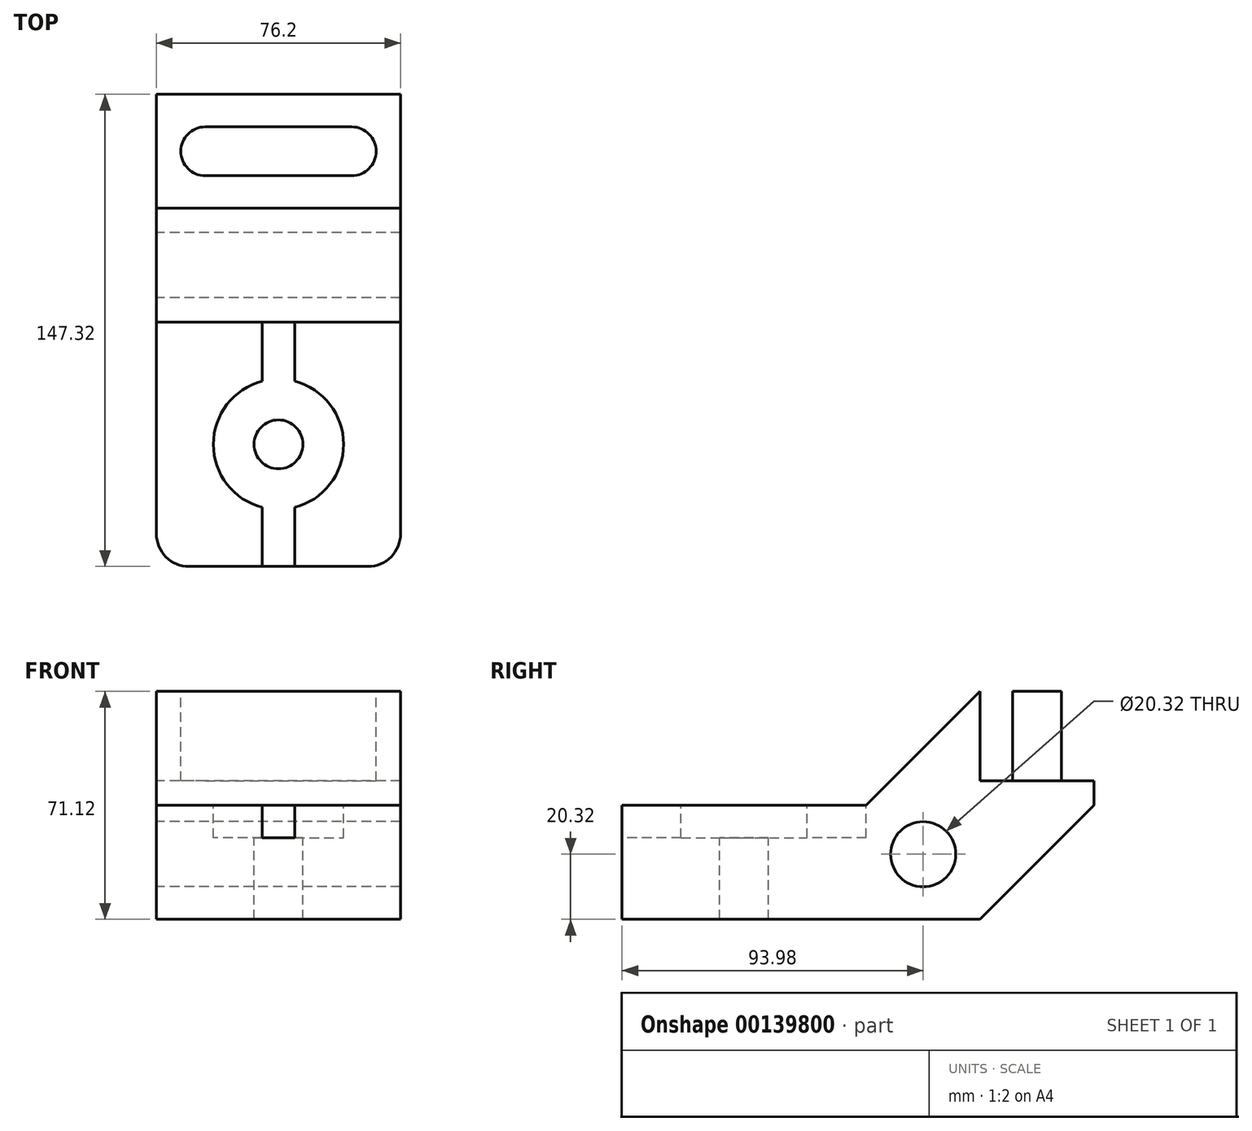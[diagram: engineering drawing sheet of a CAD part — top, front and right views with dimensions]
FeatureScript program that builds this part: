
annotation { "Feature Type Name" : "Feature", "Feature Type Description" : "" }
export const myFeature = defineFeature(function(context is Context, id is Id, definition is map)
    precondition{}
    {
        {
            var Q0;
            Q0=qCreatedBy(makeId("Right.planeOp"),FACE);
            var sketch = newSketch(context, id + "F0", { "sketchPlane" : qUnion([Q0])});
            skLineSegment(sketch, "E0.bottom", {"start": v(0, 0) * mm, "end": v(147.32, 0) * mm, "construction": true});
            skLineSegment(sketch, "E0.top", {"start": v(0, 71.12) * mm, "end": v(147.32, 71.12) * mm, "construction": true});
            skLineSegment(sketch, "E0.left", {"start": v(0, 0) * mm, "end": v(0, 71.12) * mm, "construction": true});
            skLineSegment(sketch, "E0.right", {"start": v(147.32, 0) * mm, "end": v(147.32, 71.12) * mm, "construction": true});
            skLineSegment(sketch, "E1.bottom", {"start": v(0, 0) * mm, "end": v(76.2, 0) * mm});
            skLineSegment(sketch, "E1.top", {"start": v(0, 35.56) * mm, "end": v(76.2, 35.56) * mm});
            skLineSegment(sketch, "E1.left", {"start": v(0, 0) * mm, "end": v(0, 35.56) * mm});
            skLineSegment(sketch, "E1.right", {"start": v(76.2, 0) * mm, "end": v(76.2, 35.56) * mm});
            skLineSegment(sketch, "E2.bottom", {"start": v(147.32, 0) * mm, "end": v(111.76, 0) * mm});
            skLineSegment(sketch, "E2.top", {"start": v(147.32, 71.12) * mm, "end": v(111.76, 71.12) * mm});
            skLineSegment(sketch, "E2.left", {"start": v(147.32, 0) * mm, "end": v(147.32, 71.12) * mm});
            skLineSegment(sketch, "E2.right", {"start": v(111.76, 0) * mm, "end": v(111.76, 71.12) * mm});
            skLineSegment(sketch, "E3", {"start": v(111.76, 0) * mm, "end": v(147.32, 35.56) * mm});
            skLineSegment(sketch, "E4", {"start": v(76.2, 35.56) * mm, "end": v(111.76, 71.12) * mm});
            skLineSegment(sketch, "E5", {"start": v(76.2, 0) * mm, "end": v(111.76, 0) * mm});
            skPoint(sketch, "E6", {"position": v(93.98, 20.32) * mm});
            skSolve(sketch);
        }
        {
            var Q0;
            Q0=makeQuery(id+"F0.imprint","IMPRINT",FACE,{"disambiguationData":[TD([[makeQuery(id+"F0.imprint","IMPRINT",EDGE,{"derivedFrom":sQuery(id+"F0.wireOp",EDGE,"E1.bottom")}),1.0]])]});
            var Q1;
            Q1=makeQuery(id+"F0.imprint","IMPRINT",FACE,{"disambiguationData":[TD([[makeQuery(id+"F0.imprint","IMPRINT",EDGE,{"derivedFrom":sQuery(id+"F0.wireOp",EDGE,"E1.right")}),-1.0]])]});
            var Q2;
            {var subQ0=sQuery(id+"F0.wireOp",EDGE,"E2.top");Q2=makeQuery(id+"F0.imprint","IMPRINT",FACE,{"disambiguationData":[TD([[makeQuery(id+"F0.imprint","IMPRINT",EDGE,{"derivedFrom":subQ0}),1.0]])]});}
            extrude(context, id + "F1", {"entities" : qUnion([Q0, Q1, Q2]), "depth" : 76.2 * mm});
        }
        {
            var Q0;
            Q0=sQuery(id+"F0.wireOp",VERTEX,"E6");
            var Q1;
            Q1=makeQuery(id+"F1.opExtrude","SWEPT_BODY",BODY,{"disambiguationData":[OSD([sQuery(id+"F0.wireOp",EDGE,"E1.bottom"),sQuery(id+"F0.wireOp",EDGE,"E1.top"),sQuery(id+"F0.wireOp",EDGE,"E1.left"),sQuery(id+"F0.wireOp",EDGE,"E2.top"),sQuery(id+"F0.wireOp",EDGE,"E2.left"),sQuery(id+"F0.wireOp",EDGE,"E3"),sQuery(id+"F0.wireOp",EDGE,"E4"),sQuery(id+"F0.wireOp",EDGE,"E5")])]});
            hole(context, id + "F2", {"style" : HoleStyle.SIMPLE, "endStyle" : HoleEndStyle.THROUGH, "oppositeDirection" : true, "holeDiameter" : 20.32 * mm, "locations" : qUnion([Q0]), "scope" : qUnion([Q1]), "isTappedThrough" : true});
        }
        {
            var Q0;
            Q0=makeQuery(id+"F1.opExtrude","SWEPT_FACE",FACE,{"disambiguationData":[OSD([sQuery(id+"F0.wireOp",EDGE,"E1.top")])]});
            var sketch = newSketch(context, id + "F3", { "sketchPlane" : qUnion([Q0])});
            skPoint(sketch, "E7", {"position": v(38.1, 38.1) * mm});
            skLineSegment(sketch, "E8.bottom", {"start": v(33.02, 76.2) * mm, "end": v(43.18, 76.2) * mm});
            skLineSegment(sketch, "E8.top", {"start": v(33.02, 0) * mm, "end": v(43.18, 0) * mm});
            skLineSegment(sketch, "E8.left", {"start": v(33.02, 76.2) * mm, "end": v(33.02, 0) * mm});
            skLineSegment(sketch, "E8.right", {"start": v(43.18, 76.2) * mm, "end": v(43.18, 0) * mm});
            skSolve(sketch);
        }
        {
            var Q0;
            Q0=sQuery(id+"F3.wireOp",VERTEX,"E7");
            var Q1;
            Q1=makeQuery(id+"F1.opExtrude","SWEPT_BODY",BODY,{"disambiguationData":[OSD([sQuery(id+"F0.wireOp",EDGE,"E1.bottom"),sQuery(id+"F0.wireOp",EDGE,"E1.top"),sQuery(id+"F0.wireOp",EDGE,"E1.left"),sQuery(id+"F0.wireOp",EDGE,"E2.top"),sQuery(id+"F0.wireOp",EDGE,"E2.left"),sQuery(id+"F0.wireOp",EDGE,"E3"),sQuery(id+"F0.wireOp",EDGE,"E4"),sQuery(id+"F0.wireOp",EDGE,"E5")])]});
            hole(context, id + "F4", {"style" : HoleStyle.C_BORE, "endStyle" : HoleEndStyle.THROUGH, "holeDiameter" : 15.24 * mm, "cBoreDiameter" : 40.64 * mm, "cBoreDepth" : 10.16 * mm, "locations" : qUnion([Q0]), "scope" : qUnion([Q1]), "isTappedThrough" : true});
        }
        {
            var Q0;
            Q0=makeQuery(id+"F3.imprint","IMPRINT",FACE,{"disambiguationData":[TD([[makeQuery(id+"F3.imprint","IMPRINT",EDGE,{"derivedFrom":sQuery(id+"F3.wireOp",EDGE,"E8.bottom")}),1.0]])]});
            extrude(context, id + "F5", {"entities" : qUnion([Q0]), "operationType" : NewBodyOperationType.REMOVE, "oppositeDirection" : true, "depth" : 10.16 * mm});
        }
        {
            var Q0;
            Q0=makeQuery(id+"F1.opExtrude","SWEPT_FACE",FACE,{"disambiguationData":[OSD([sQuery(id+"F0.wireOp",EDGE,"E2.top")])]});
            var sketch = newSketch(context, id + "F6", { "sketchPlane" : qUnion([Q0])});
            skLineSegment(sketch, "E9", {"start": v(15.24, 129.54) * mm, "end": v(60.96, 129.54) * mm, "construction": true});
            skArc(sketch, "E10.0.startCap", {"start": v(15.24, 121.92) * mm, "mid": v(7.62, 129.54) * mm, "end": v(15.24, 137.16) * mm});
            skArc(sketch, "E10.0.endCap", {"start": v(60.96, 137.16) * mm, "mid": v(68.58, 129.54) * mm, "end": v(60.96, 121.92) * mm});
            skLineSegment(sketch, "E10.0.left", {"start": v(15.24, 137.16) * mm, "end": v(60.96, 137.16) * mm});
            skLineSegment(sketch, "E10.0.right", {"start": v(15.24, 121.92) * mm, "end": v(60.96, 121.92) * mm});
            skSolve(sketch);
        }
        {
            var Q0;
            Q0=makeQuery(id+"F6.imprint","IMPRINT",FACE,{"disambiguationData":[TD([[makeQuery(id+"F6.imprint","IMPRINT",EDGE,{"derivedFrom":sQuery(id+"F6.wireOp",EDGE,"E10.0.startCap")}),-1.0]])]});
            extrude(context, id + "F7", {"entities" : qUnion([Q0]), "operationType" : NewBodyOperationType.REMOVE, "oppositeDirection" : true, "depth" : 27.94 * mm});
        }
        {
            var Q0;
            Q0=makeQuery(id+"F1.opExtrude","CAP_EDGE",EDGE,{"disambiguationData":[OSD([sQuery(id+"F0.wireOp",EDGE,"E1.left")])],"isStart":true});
            var Q1;
            Q1=makeQuery(id+"F1.opExtrude","CAP_EDGE",EDGE,{"disambiguationData":[OSD([sQuery(id+"F0.wireOp",EDGE,"E1.left")])],"isStart":false});
            fillet(context, id + "F8", {"entities" : qUnion([Q0, Q1]), "radius" : 10.16 * mm, "tangentPropagation" : true, "allowEdgeOverflow" : false});
        }
    });
